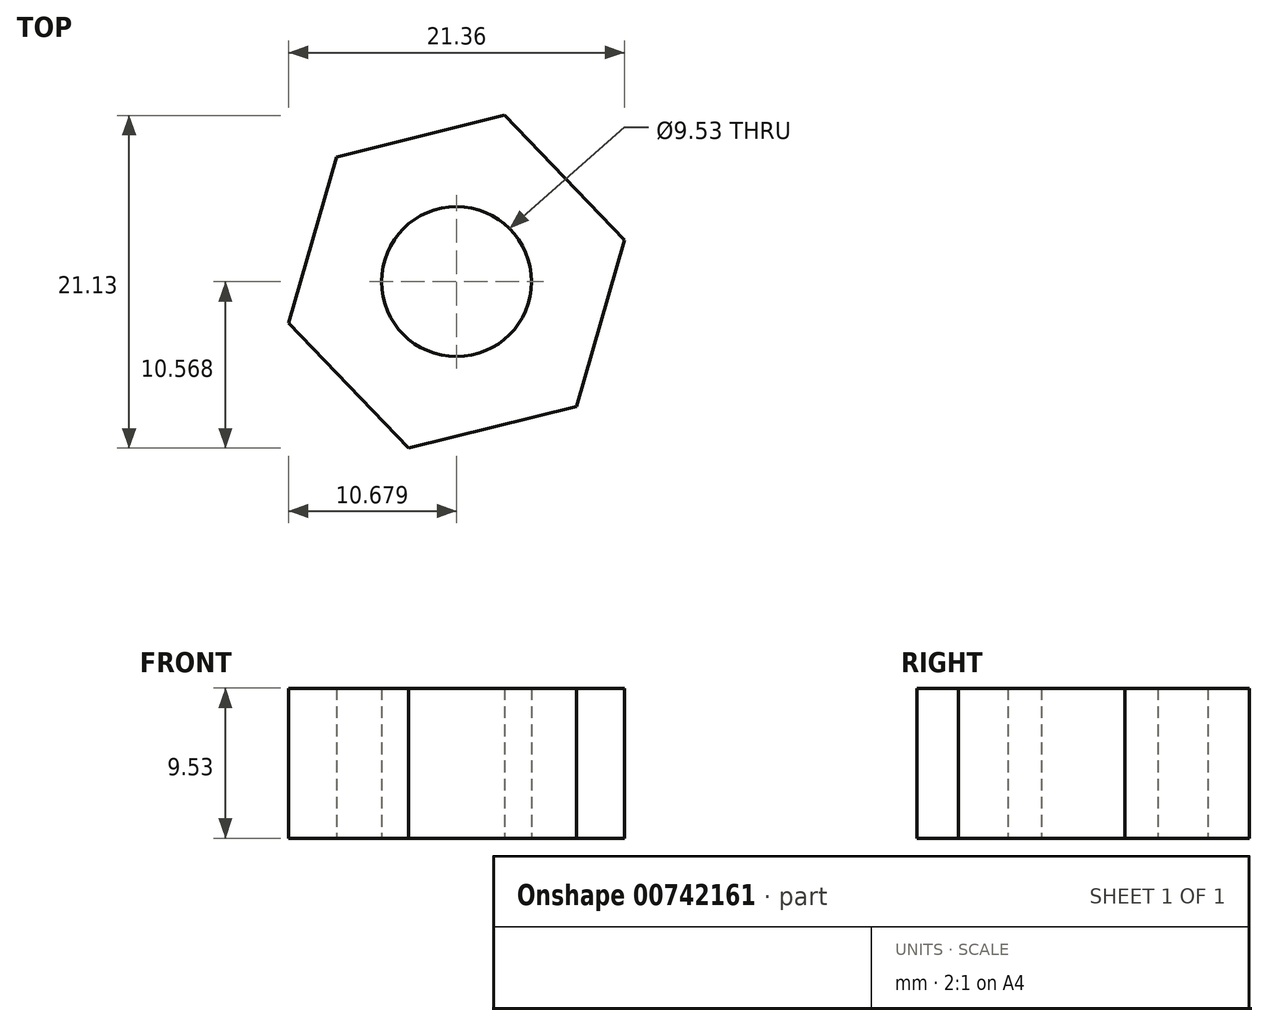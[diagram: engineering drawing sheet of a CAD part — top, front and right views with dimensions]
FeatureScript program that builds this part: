
annotation { "Feature Type Name" : "Feature", "Feature Type Description" : "" }
export const myFeature = defineFeature(function(context is Context, id is Id, definition is map)
    precondition{}
    {
        {
            var Q0;
            Q0=qCreatedBy(makeId("Top.planeOp"),FACE);
            var sketch = newSketch(context, id + "F0", { "sketchPlane" : qUnion([Q0])});
            skCircle(sketch, "E0.cCircle", {"center": v(-9.15, -4.74) * mm, "radius": 9.53 * mm, "construction": true});
            skLineSegment(sketch, "E0.0", {"start": v(1.53, -2.1) * mm, "end": v(-1.53, -12.67) * mm});
            skLineSegment(sketch, "E0.1", {"start": v(-1.53, -12.67) * mm, "end": v(-12.2, -15.3) * mm});
            skLineSegment(sketch, "E0.2", {"start": v(-12.2, -15.3) * mm, "end": v(-19.83, -7.38) * mm});
            skLineSegment(sketch, "E0.3", {"start": v(-19.83, -7.38) * mm, "end": v(-16.78, 3.18) * mm});
            skLineSegment(sketch, "E0.4", {"start": v(-16.78, 3.18) * mm, "end": v(-6.1, 5.82) * mm});
            skLineSegment(sketch, "E0.5", {"start": v(-6.1, 5.82) * mm, "end": v(1.53, -2.1) * mm});
            skPoint(sketch, "E0.0.midPoint", {"position": v(0, -7.38) * mm});
            skCircle(sketch, "E1", {"center": v(-9.15, -4.74) * mm, "radius": 4.76 * mm});
            skSolve(sketch);
        }
        {
            var Q0;
            Q0 = qSketchRegion(id + "F0", true);
            extrude(context, id + "F1", {"entities" : qUnion([Q0]), "depth" : 9.52 * mm, "offsetDistance" : 25.4 * mm});
        }
    });
